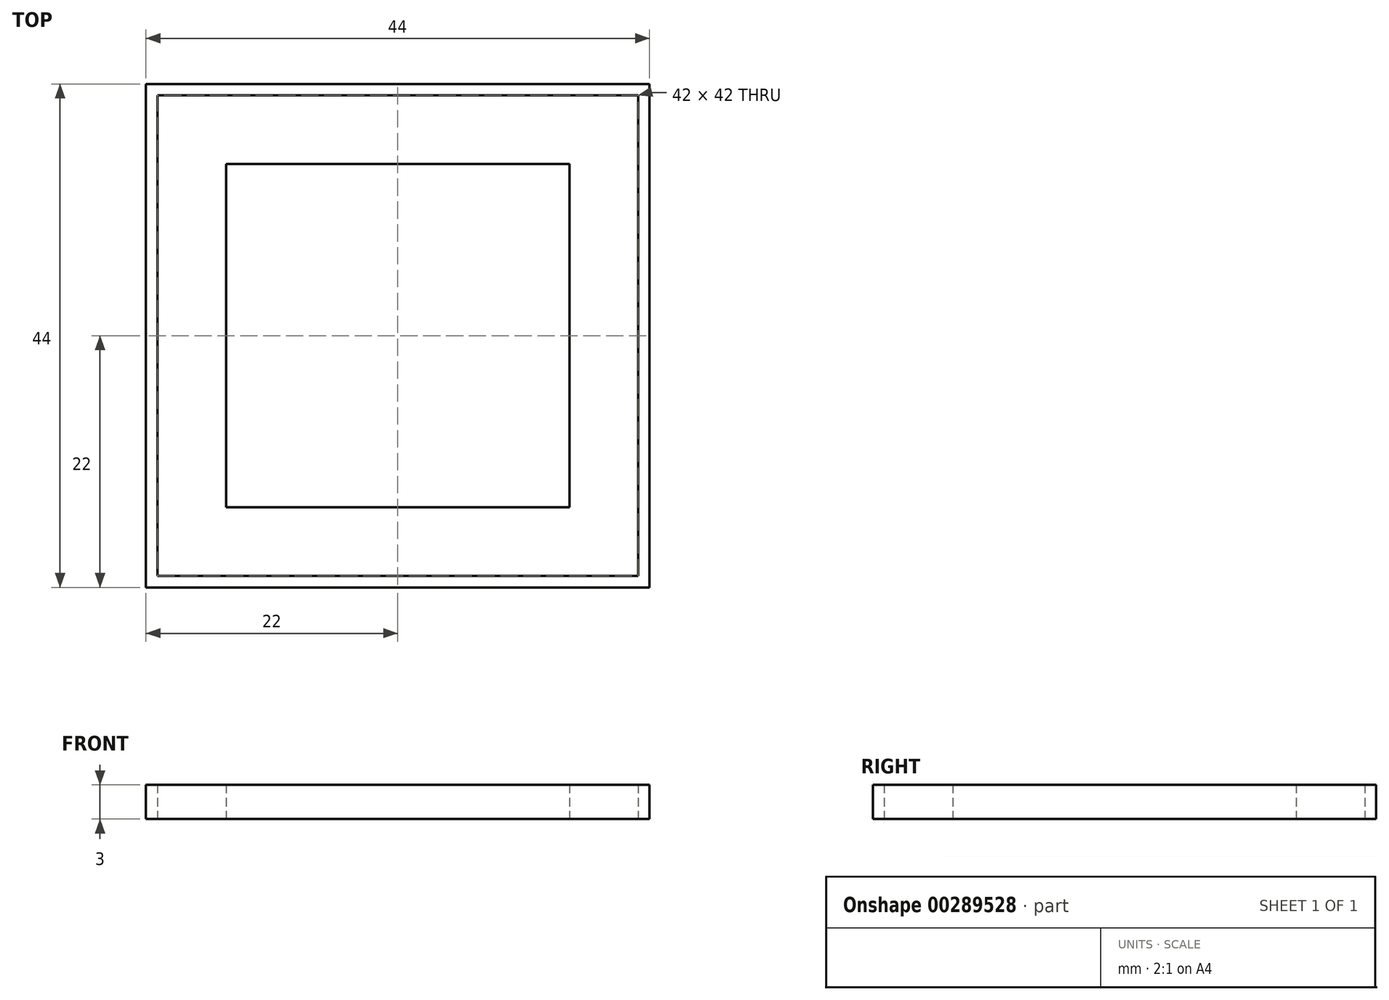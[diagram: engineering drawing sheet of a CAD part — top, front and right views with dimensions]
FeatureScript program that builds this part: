
annotation { "Feature Type Name" : "Feature", "Feature Type Description" : "" }
export const myFeature = defineFeature(function(context is Context, id is Id, definition is map)
    precondition{}
    {
        {
            var Q0;
            Q0=qCreatedBy(makeId("Top.planeOp"),FACE);
            var sketch = newSketch(context, id + "F0", { "sketchPlane" : qUnion([Q0])});
            skLineSegment(sketch, "E0.bottom", {"start": v(15, 15) * mm, "end": v(-15, 15) * mm});
            skLineSegment(sketch, "E0.top", {"start": v(15, -15) * mm, "end": v(-15, -15) * mm});
            skLineSegment(sketch, "E0.left", {"start": v(15, 15) * mm, "end": v(15, -15) * mm});
            skLineSegment(sketch, "E0.right", {"start": v(-15, 15) * mm, "end": v(-15, -15) * mm});
            skPoint(sketch, "E0.middle", {"position": v(0, 0) * mm});
            skLineSegment(sketch, "E1.bottom", {"start": v(21, 21) * mm, "end": v(-21, 21) * mm});
            skLineSegment(sketch, "E1.top", {"start": v(21, -21) * mm, "end": v(-21, -21) * mm});
            skLineSegment(sketch, "E1.left", {"start": v(21, 21) * mm, "end": v(21, -21) * mm});
            skLineSegment(sketch, "E1.right", {"start": v(-21, 21) * mm, "end": v(-21, -21) * mm});
            skLineSegment(sketch, "E2.bottom", {"start": v(22, 22) * mm, "end": v(-22, 22) * mm});
            skLineSegment(sketch, "E2.top", {"start": v(22, -22) * mm, "end": v(-22, -22) * mm});
            skLineSegment(sketch, "E2.left", {"start": v(22, 22) * mm, "end": v(22, -22) * mm});
            skLineSegment(sketch, "E2.right", {"start": v(-22, 22) * mm, "end": v(-22, -22) * mm});
            skSolve(sketch);
        }
        {
            var Q0;
            Q0 = qSketchRegion(id + "F0", true);
            var Q1;
            Q1=makeQuery(id+"F0.imprint","IMPRINT",FACE,{"disambiguationData":[TD([[makeQuery(id+"F0.imprint","IMPRINT",EDGE,{"derivedFrom":sQuery(id+"F0.wireOp",EDGE,"E0.bottom")}),1.0]])]});
            extrude(context, id + "F1", {"entities" : qUnion([Q0, Q1]), "depth" : 3 * mm});
        }
        {
            var Q0;
            Q0 = qSketchRegion(id + "F0", true);
            extrude(context, id + "F2", {"entities" : qUnion([Q0]), "operationType" : NewBodyOperationType.ADD, "depth" : 3 * mm});
        }
    });
